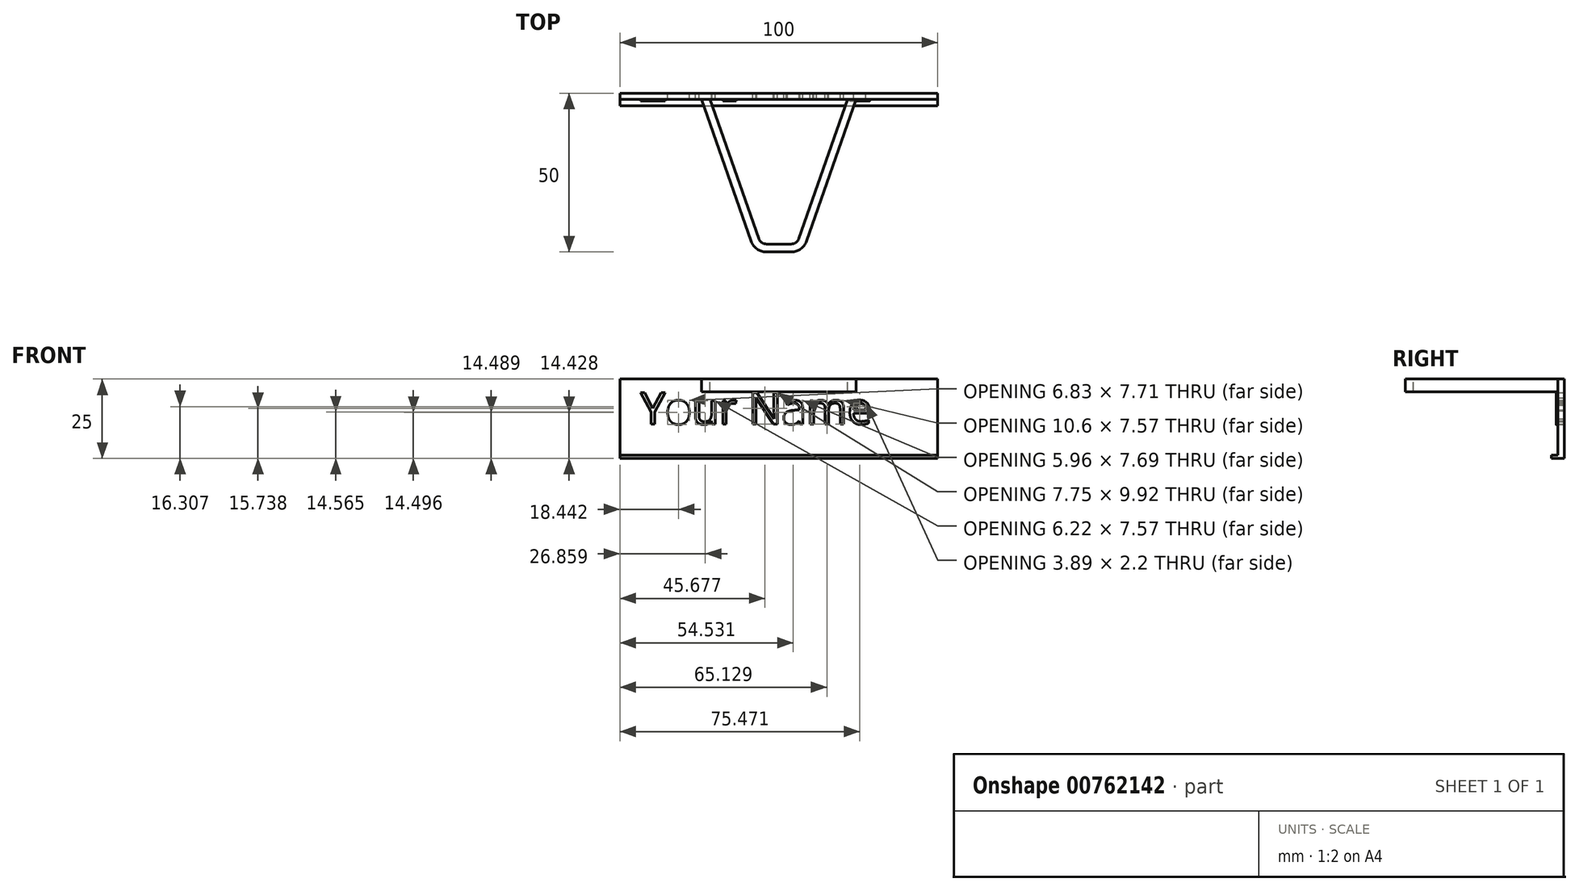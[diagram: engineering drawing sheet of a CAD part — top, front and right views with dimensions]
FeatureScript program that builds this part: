
annotation { "Feature Type Name" : "Feature", "Feature Type Description" : "" }
export const myFeature = defineFeature(function(context is Context, id is Id, definition is map)
    precondition{}
    {
        {
            var Q0;
            Q0=qCreatedBy(makeId("Front.planeOp"),FACE);
            var sketch = newSketch(context, id + "F0", { "sketchPlane" : qUnion([Q0])});
            skLineSegment(sketch, "E0.bottom", {"start": v(0, 0) * mm, "end": v(-100, 0) * mm});
            skLineSegment(sketch, "E0.top", {"start": v(0, 25) * mm, "end": v(-100, 25) * mm});
            skLineSegment(sketch, "E0.left", {"start": v(0, 0) * mm, "end": v(0, 25) * mm});
            skLineSegment(sketch, "E0.right", {"start": v(-100, 0) * mm, "end": v(-100, 25) * mm});
            skLineSegment(sketch, "E1", {"start": v(-100, 1) * mm, "end": v(0, 1) * mm});
            skLineSegment(sketch, "E2", {"start": v(-100, 23) * mm, "end": v(0, 23) * mm});
            skText(sketch, "E3", { "text": "Your Name", "fontName": "OpenSans-Regular.ttf"});
            const initialGuessF0  = {"E3": [-0.09353, 0.01078, 1, 0, 0.01]};
            skSetInitialGuess(sketch, initialGuessF0);
            skSolve(sketch);
        }
        {
            var Q0;
            {var subQ1=sQuery(id+"F0.wireOp",EDGE,"E1");Q0=makeQuery(id+"F0.imprint","IMPRINT",FACE,{"disambiguationData":[TD([[makeQuery(id+"F0.imprint","IMPRINT",EDGE,{"derivedFrom":subQ1}),1.0]])]});}
            var Q1;
            Q1=makeQuery(id+"F0.imprint","IMPRINT",FACE,{"disambiguationData":[TD([[makeQuery(id+"F0.imprint","IMPRINT",EDGE,{"derivedFrom":sQuery(id+"F0.wireOp",EDGE,"E3.sketch_text.stroke-199")}),1.0]])]});
            var Q2;
            Q2=makeQuery(id+"F0.imprint","IMPRINT",FACE,{"disambiguationData":[TD([[makeQuery(id+"F0.imprint","IMPRINT",EDGE,{"derivedFrom":sQuery(id+"F0.wireOp",EDGE,"E3.sketch_text.stroke-170")}),-1.0]])]});
            var Q3;
            Q3=makeQuery(id+"F0.imprint","IMPRINT",FACE,{"disambiguationData":[TD([[makeQuery(id+"F0.imprint","IMPRINT",EDGE,{"derivedFrom":sQuery(id+"F0.wireOp",EDGE,"E3.sketch_text.stroke-208")}),1.0]])]});
            var Q4;
            Q4=makeQuery(id+"F0.imprint","IMPRINT",FACE,{"disambiguationData":[TD([[makeQuery(id+"F0.imprint","IMPRINT",EDGE,{"derivedFrom":sQuery(id+"F0.wireOp",EDGE,"E3.sketch_text.stroke-153")}),-1.0]])]});
            var Q5;
            Q5=makeQuery(id+"F0.imprint","IMPRINT",FACE,{"disambiguationData":[TD([[makeQuery(id+"F0.imprint","IMPRINT",EDGE,{"derivedFrom":sQuery(id+"F0.wireOp",EDGE,"E3.sketch_text.stroke-126")}),-1.0]])]});
            var Q6;
            Q6=makeQuery(id+"F0.imprint","IMPRINT",FACE,{"disambiguationData":[TD([[makeQuery(id+"F0.imprint","IMPRINT",EDGE,{"derivedFrom":sQuery(id+"F0.wireOp",EDGE,"E3.sketch_text.stroke-145")}),1.0]])]});
            var Q7;
            Q7=makeQuery(id+"F0.imprint","IMPRINT",FACE,{"disambiguationData":[TD([[makeQuery(id+"F0.imprint","IMPRINT",EDGE,{"derivedFrom":sQuery(id+"F0.wireOp",EDGE,"E3.sketch_text.stroke-114")}),-1.0]])]});
            var Q8;
            Q8=makeQuery(id+"F0.imprint","IMPRINT",FACE,{"disambiguationData":[TD([[makeQuery(id+"F0.imprint","IMPRINT",EDGE,{"derivedFrom":sQuery(id+"F0.wireOp",EDGE,"E3.sketch_text.stroke-106")}),-1.0]])]});
            var Q9;
            Q9=makeQuery(id+"F0.imprint","IMPRINT",FACE,{"disambiguationData":[TD([[makeQuery(id+"F0.imprint","IMPRINT",EDGE,{"derivedFrom":sQuery(id+"F0.wireOp",EDGE,"E3.sketch_text.stroke-99")}),1.0]])]});
            var Q10;
            Q10=makeQuery(id+"F0.imprint","IMPRINT",FACE,{"disambiguationData":[TD([[makeQuery(id+"F0.imprint","IMPRINT",EDGE,{"derivedFrom":sQuery(id+"F0.wireOp",EDGE,"E3.sketch_text.stroke-88")}),-1.0]])]});
            var Q11;
            Q11=makeQuery(id+"F0.imprint","IMPRINT",FACE,{"disambiguationData":[TD([[makeQuery(id+"F0.imprint","IMPRINT",EDGE,{"derivedFrom":sQuery(id+"F0.wireOp",EDGE,"E3.sketch_text.stroke-80")}),1.0]])]});
            var Q12;
            Q12=makeQuery(id+"F0.imprint","IMPRINT",FACE,{"disambiguationData":[TD([[makeQuery(id+"F0.imprint","IMPRINT",EDGE,{"derivedFrom":sQuery(id+"F0.wireOp",EDGE,"E3.sketch_text.stroke-61")}),-1.0]])]});
            var Q13;
            Q13=makeQuery(id+"F0.imprint","IMPRINT",FACE,{"disambiguationData":[TD([[makeQuery(id+"F0.imprint","IMPRINT",EDGE,{"derivedFrom":sQuery(id+"F0.wireOp",EDGE,"E3.sketch_text.stroke-37")}),1.0]])]});
            var Q14;
            Q14=makeQuery(id+"F0.imprint","IMPRINT",FACE,{"disambiguationData":[TD([[makeQuery(id+"F0.imprint","IMPRINT",EDGE,{"derivedFrom":sQuery(id+"F0.wireOp",EDGE,"E3.sketch_text.stroke-18")}),-1.0]])]});
            var Q15;
            Q15=makeQuery(id+"F0.imprint","IMPRINT",FACE,{"disambiguationData":[TD([[makeQuery(id+"F0.imprint","IMPRINT",EDGE,{"derivedFrom":sQuery(id+"F0.wireOp",EDGE,"E3.sketch_text.stroke-45")}),-1.0]])]});
            var Q16;
            Q16=makeQuery(id+"F0.imprint","IMPRINT",FACE,{"disambiguationData":[TD([[makeQuery(id+"F0.imprint","IMPRINT",EDGE,{"derivedFrom":sQuery(id+"F0.wireOp",EDGE,"E3.sketch_text.stroke-0")}),-1.0]])]});
            var Q17;
            {var subQ0=sQuery(id+"F0.wireOp",EDGE,"E0.top");Q17=makeQuery(id+"F0.imprint","IMPRINT",FACE,{"disambiguationData":[TD([[makeQuery(id+"F0.imprint","IMPRINT",EDGE,{"derivedFrom":subQ0}),1.0]])]});}
            extrude(context, id + "F1", {"entities" : qUnion([Q0, Q1, Q2, Q3, Q4, Q5, Q6, Q7, Q8, Q9, Q10, Q11, Q12, Q13, Q14, Q15, Q16, Q17]), "depth" : 2 * mm, "offsetDistance" : 25 * mm});
        }
        {
            var Q0;
            {var subQ0=sQuery(id+"F0.wireOp",EDGE,"E0.bottom");Q0=makeQuery(id+"F0.imprint","IMPRINT",FACE,{"disambiguationData":[TD([[makeQuery(id+"F0.imprint","IMPRINT",EDGE,{"derivedFrom":subQ0}),-1.0]])]});}
            extrude(context, id + "F2", {"entities" : qUnion([Q0]), "operationType" : NewBodyOperationType.ADD, "depth" : 4 * mm, "offsetDistance" : 25 * mm});
        }
        {
            var Q0;
            Q0=makeQuery(id+"F1.opExtrude","SWEPT_FACE",FACE,{"disambiguationData":[OSD([sQuery(id+"F0.wireOp",EDGE,"E0.top")])]});
            var sketch = newSketch(context, id + "F3", { "sketchPlane" : qUnion([Q0])});
            skLineSegment(sketch, "E4", {"start": v(-50, 0) * mm, "end": v(-50, -66.3) * mm, "construction": true});
            skLineSegment(sketch, "E5", {"start": v(-25, 0) * mm, "end": v(-41.33, -46.65) * mm});
            skLineSegment(sketch, "E6", {"start": v(-46.05, -50) * mm, "end": v(-53.95, -50) * mm});
            skLineSegment(sketch, "E7", {"start": v(-58.67, -46.65) * mm, "end": v(-75, 0) * mm});
            skPoint(sketch, "E8.visualSharp", {"position": v(-42.5, -50) * mm});
            skArc(sketch, "E8.filletArc", {"start": v(-46.05, -50) * mm, "mid": v(-43.15, -49.08) * mm, "end": v(-41.33, -46.65) * mm});
            skPoint(sketch, "E9.visualSharp", {"position": v(-57.5, -50) * mm});
            skArc(sketch, "E9.filletArc", {"start": v(-58.67, -46.65) * mm, "mid": v(-56.85, -49.08) * mm, "end": v(-53.95, -50) * mm});
            skLineSegment(sketch, "E10.0", {"start": v(-56.31, -45.83) * mm, "end": v(-72.64, 0.83) * mm});
            skLineSegment(sketch, "E10.1", {"start": v(-27.36, 0.83) * mm, "end": v(-43.69, -45.83) * mm});
            skArc(sketch, "E10.2", {"start": v(-46.05, -47.5) * mm, "mid": v(-44.6, -47.04) * mm, "end": v(-43.69, -45.83) * mm});
            skLineSegment(sketch, "E10.3", {"start": v(-46.05, -47.5) * mm, "end": v(-53.95, -47.5) * mm});
            skArc(sketch, "E10.4", {"start": v(-56.31, -45.83) * mm, "mid": v(-55.4, -47.04) * mm, "end": v(-53.95, -47.5) * mm});
            skSolve(sketch);
        }
        {
            var Q0;
            Q0=makeQuery(id+"F3.imprint","IMPRINT",FACE,{"disambiguationData":[TD([[makeQuery(id+"F3.imprint","IMPRINT",EDGE,{"derivedFrom":sQuery(id+"F3.wireOp",EDGE,"E6")}),-1.0]])]});
            extrude(context, id + "F4", {"entities" : qUnion([Q0]), "oppositeDirection" : true, "depth" : 4 * mm, "offsetDistance" : 25 * mm});
        }
        {
            var Q0;
            Q0=makeQuery(id+"F0.imprint","IMPRINT",FACE,{"disambiguationData":[TD([[makeQuery(id+"F0.imprint","IMPRINT",EDGE,{"derivedFrom":sQuery(id+"F0.wireOp",EDGE,"E3.sketch_text.stroke-0")}),-1.0]])]});
            var Q1;
            Q1=makeQuery(id+"F0.imprint","IMPRINT",FACE,{"disambiguationData":[TD([[makeQuery(id+"F0.imprint","IMPRINT",EDGE,{"derivedFrom":sQuery(id+"F0.wireOp",EDGE,"E3.sketch_text.stroke-18")}),-1.0]])]});
            var Q2;
            Q2=makeQuery(id+"F0.imprint","IMPRINT",FACE,{"disambiguationData":[TD([[makeQuery(id+"F0.imprint","IMPRINT",EDGE,{"derivedFrom":sQuery(id+"F0.wireOp",EDGE,"E3.sketch_text.stroke-45")}),-1.0]])]});
            var Q3;
            Q3=makeQuery(id+"F0.imprint","IMPRINT",FACE,{"disambiguationData":[TD([[makeQuery(id+"F0.imprint","IMPRINT",EDGE,{"derivedFrom":sQuery(id+"F0.wireOp",EDGE,"E3.sketch_text.stroke-61")}),-1.0]])]});
            var Q4;
            Q4=makeQuery(id+"F0.imprint","IMPRINT",FACE,{"disambiguationData":[TD([[makeQuery(id+"F0.imprint","IMPRINT",EDGE,{"derivedFrom":sQuery(id+"F0.wireOp",EDGE,"E3.sketch_text.stroke-88")}),-1.0]])]});
            var Q5;
            Q5=makeQuery(id+"F0.imprint","IMPRINT",FACE,{"disambiguationData":[TD([[makeQuery(id+"F0.imprint","IMPRINT",EDGE,{"derivedFrom":sQuery(id+"F0.wireOp",EDGE,"E3.sketch_text.stroke-106")}),-1.0]])]});
            var Q6;
            Q6=makeQuery(id+"F0.imprint","IMPRINT",FACE,{"disambiguationData":[TD([[makeQuery(id+"F0.imprint","IMPRINT",EDGE,{"derivedFrom":sQuery(id+"F0.wireOp",EDGE,"E3.sketch_text.stroke-114")}),-1.0]])]});
            var Q7;
            Q7=makeQuery(id+"F0.imprint","IMPRINT",FACE,{"disambiguationData":[TD([[makeQuery(id+"F0.imprint","IMPRINT",EDGE,{"derivedFrom":sQuery(id+"F0.wireOp",EDGE,"E3.sketch_text.stroke-126")}),-1.0]])]});
            var Q8;
            Q8=makeQuery(id+"F0.imprint","IMPRINT",FACE,{"disambiguationData":[TD([[makeQuery(id+"F0.imprint","IMPRINT",EDGE,{"derivedFrom":sQuery(id+"F0.wireOp",EDGE,"E3.sketch_text.stroke-153")}),-1.0]])]});
            var Q9;
            Q9=makeQuery(id+"F0.imprint","IMPRINT",FACE,{"disambiguationData":[TD([[makeQuery(id+"F0.imprint","IMPRINT",EDGE,{"derivedFrom":sQuery(id+"F0.wireOp",EDGE,"E3.sketch_text.stroke-170")}),-1.0]])]});
            extrude(context, id + "F5", {"entities" : qUnion([Q0, Q1, Q2, Q3, Q4, Q5, Q6, Q7, Q8, Q9]), "operationType" : NewBodyOperationType.ADD, "depth" : 2.5 * mm, "offsetDistance" : 25 * mm});
        }
    });
